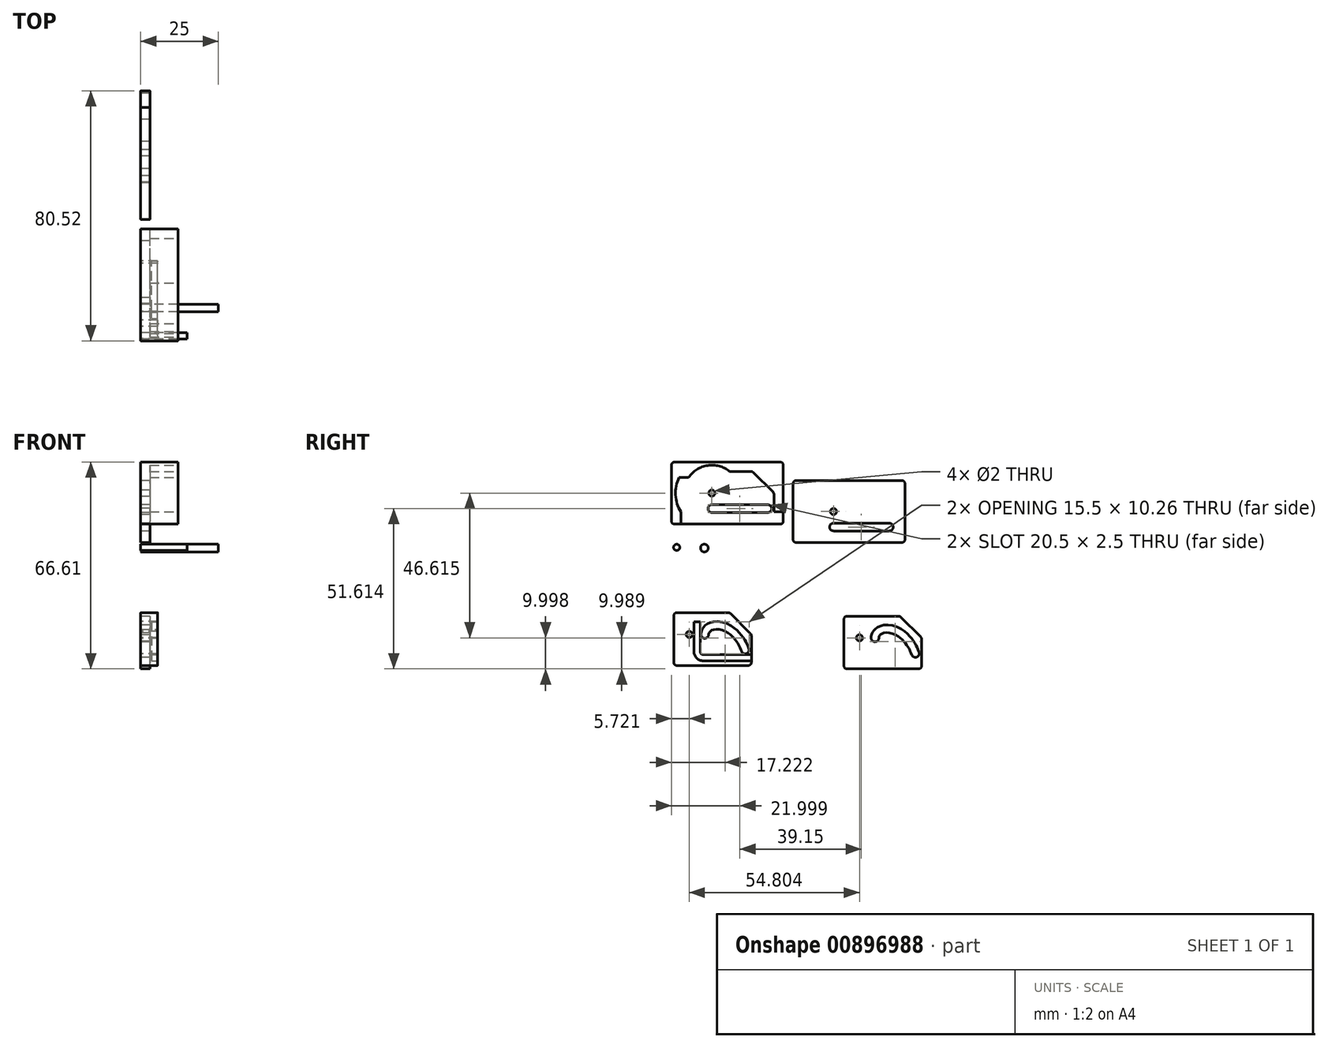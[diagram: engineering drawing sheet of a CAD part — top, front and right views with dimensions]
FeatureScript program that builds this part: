
annotation { "Feature Type Name" : "Feature", "Feature Type Description" : "" }
export const myFeature = defineFeature(function(context is Context, id is Id, definition is map)
    precondition{}
    {
        {
            var Q0;
            Q0=qCreatedBy(makeId("Right.planeOp"),FACE);
            var sketch = newSketch(context, id + "F0", { "sketchPlane" : qUnion([Q0])});
            skLineSegment(sketch, "E0.bottom", {"start": v(-142.35, 68.58) * mm, "end": v(-108.35, 68.58) * mm});
            skLineSegment(sketch, "E0.top", {"start": v(-142.35, 48.58) * mm, "end": v(-108.35, 48.58) * mm});
            skLineSegment(sketch, "E0.left", {"start": v(-143.35, 67.58) * mm, "end": v(-143.35, 49.58) * mm});
            skLineSegment(sketch, "E0.right", {"start": v(-107.35, 67.58) * mm, "end": v(-107.35, 49.58) * mm});
            skLineSegment(sketch, "E1", {"start": v(-130.35, 53.58) * mm, "end": v(-112.35, 53.58) * mm, "construction": true});
            skCircle(sketch, "E2", {"center": v(-130.35, 58.58) * mm, "radius": 1 * mm});
            skArc(sketch, "E3.0.startCap", {"start": v(-130.35, 52.33) * mm, "mid": v(-131.6, 53.58) * mm, "end": v(-130.35, 54.83) * mm});
            skArc(sketch, "E3.0.endCap", {"start": v(-112.35, 54.83) * mm, "mid": v(-111.1, 53.58) * mm, "end": v(-112.35, 52.33) * mm});
            skLineSegment(sketch, "E3.0.left", {"start": v(-130.35, 54.83) * mm, "end": v(-112.35, 54.83) * mm});
            skLineSegment(sketch, "E3.0.right", {"start": v(-130.35, 52.33) * mm, "end": v(-112.35, 52.33) * mm});
            skCircle(sketch, "E4", {"center": v(-176.78, 19) * mm, "radius": 1 * mm});
            skLineSegment(sketch, "E5", {"start": v(-180.78, 9) * mm, "end": v(-157.78, 9) * mm});
            skLineSegment(sketch, "E6", {"start": v(-181.78, 10) * mm, "end": v(-181.78, 25) * mm});
            skLineSegment(sketch, "E7", {"start": v(-180.78, 26) * mm, "end": v(-164.2, 26) * mm});
            skLineSegment(sketch, "E8", {"start": v(-156.78, 18.59) * mm, "end": v(-156.78, 10) * mm});
            skPoint(sketch, "E9", {"position": v(-171.78, 19) * mm});
            skPoint(sketch, "E10", {"position": v(-171.71, 19.56) * mm});
            skPoint(sketch, "E11", {"position": v(-171.5, 20.1) * mm});
            skPoint(sketch, "E12", {"position": v(-171.17, 20.6) * mm});
            skPoint(sketch, "E13", {"position": v(-170.71, 21.05) * mm});
            skPoint(sketch, "E14", {"position": v(-170.13, 21.42) * mm});
            skPoint(sketch, "E15", {"position": v(-169.45, 21.7) * mm});
            skPoint(sketch, "E16", {"position": v(-168.67, 21.87) * mm});
            skPoint(sketch, "E17", {"position": v(-167.8, 21.91) * mm});
            skPoint(sketch, "E18", {"position": v(-166.88, 21.83) * mm});
            skPoint(sketch, "E19", {"position": v(-165.9, 21.6) * mm});
            skPoint(sketch, "E20", {"position": v(-164.9, 21.21) * mm});
            skPoint(sketch, "E21", {"position": v(-163.89, 20.67) * mm});
            skPoint(sketch, "E22", {"position": v(-162.88, 19.96) * mm});
            skPoint(sketch, "E23", {"position": v(-161.91, 19.09) * mm});
            skPoint(sketch, "E24", {"position": v(-161, 18.05) * mm});
            skPoint(sketch, "E25", {"position": v(-160.15, 16.85) * mm});
            skPoint(sketch, "E26", {"position": v(-159.4, 15.5) * mm});
            skPoint(sketch, "E27", {"position": v(-158.78, 14) * mm});
            skFitSpline(sketch, "E28", {"points": [v(-171.78, 19) * mm, v(-171.71, 19.56) * mm, v(-171.5, 20.1) * mm, v(-171.17, 20.6) * mm, v(-170.71, 21.05) * mm, v(-170.13, 21.42) * mm, v(-169.45, 21.7) * mm, v(-168.67, 21.87) * mm, v(-167.8, 21.91) * mm, v(-166.88, 21.83) * mm, v(-165.9, 21.6) * mm, v(-164.9, 21.21) * mm, v(-163.89, 20.67) * mm, v(-162.88, 19.96) * mm, v(-161.91, 19.09) * mm, v(-161, 18.05) * mm, v(-160.15, 16.85) * mm, v(-159.4, 15.5) * mm, v(-158.78, 14) * mm], "startDerivative": vector(0.94, 13.4) * mm, "endDerivative": vector(8.38, -21.3) * mm});
            skArc(sketch, "E29.0.startCap", {"start": v(-170.53, 18.91) * mm, "mid": v(-171.87, 17.75) * mm, "end": v(-173.03, 19.09) * mm});
            skArc(sketch, "E29.0.endCap", {"start": v(-157.62, 14.46) * mm, "mid": v(-158.32, 12.84) * mm, "end": v(-159.94, 13.54) * mm});
            skFitSpline(sketch, "E29.0.left", {"points": [v(-173.03, 19.09) * mm, v(-173.02, 19.12) * mm, v(-173.02, 19.2) * mm, v(-173, 19.32) * mm, v(-173, 19.46) * mm, v(-172.97, 19.6) * mm, v(-172.95, 19.73) * mm, v(-172.94, 19.81) * mm, v(-172.92, 19.87) * mm, v(-172.9, 19.94) * mm, v(-172.88, 20.02) * mm, v(-172.85, 20.13) * mm, v(-172.79, 20.31) * mm, v(-172.71, 20.49) * mm, v(-172.64, 20.63) * mm, v(-172.6, 20.72) * mm, v(-172.5, 20.88) * mm, v(-172.37, 21.1) * mm, v(-172.21, 21.31) * mm, v(-172.07, 21.47) * mm, v(-171.93, 21.63) * mm, v(-171.75, 21.81) * mm, v(-171.5, 22.02) * mm, v(-171.18, 22.26) * mm, v(-170.73, 22.53) * mm, v(-170.16, 22.79) * mm, v(-169.56, 22.97) * mm, v(-168.74, 23.14) * mm, v(-167.69, 23.2) * mm, v(-166.4, 23.05) * mm, v(-165.14, 22.7) * mm, v(-163.9, 22.15) * mm, v(-162.93, 21.56) * mm, v(-162.18, 21) * mm, v(-161.64, 20.56) * mm, v(-161.12, 20.07) * mm, v(-160.62, 19.56) * mm, v(-160.23, 19.1) * mm, v(-159.93, 18.72) * mm, v(-159.63, 18.33) * mm, v(-159.35, 17.92) * mm, v(-159.09, 17.5) * mm, v(-158.9, 17.19) * mm, v(-158.7, 16.86) * mm, v(-158.52, 16.53) * mm, v(-158.38, 16.24) * mm, v(-158.26, 16) * mm, v(-158.16, 15.77) * mm, v(-158.03, 15.48) * mm, v(-157.84, 15.02) * mm, v(-157.7, 14.68) * mm, v(-157.62, 14.46) * mm]});
            skFitSpline(sketch, "E29.0.right", {"points": [v(-170.53, 18.91) * mm, v(-170.53, 18.95) * mm, v(-170.53, 19.01) * mm, v(-170.52, 19.1) * mm, v(-170.51, 19.17) * mm, v(-170.5, 19.23) * mm, v(-170.5, 19.26) * mm, v(-170.5, 19.28) * mm, v(-170.5, 19.3) * mm, v(-170.49, 19.3) * mm, v(-170.48, 19.32) * mm, v(-170.47, 19.35) * mm, v(-170.46, 19.4) * mm, v(-170.43, 19.46) * mm, v(-170.4, 19.5) * mm, v(-170.4, 19.54) * mm, v(-170.37, 19.58) * mm, v(-170.34, 19.64) * mm, v(-170.3, 19.7) * mm, v(-170.24, 19.77) * mm, v(-170.2, 19.83) * mm, v(-170.13, 19.9) * mm, v(-170.06, 19.97) * mm, v(-169.95, 20.06) * mm, v(-169.8, 20.17) * mm, v(-169.58, 20.3) * mm, v(-169.28, 20.44) * mm, v(-168.94, 20.55) * mm, v(-168.45, 20.65) * mm, v(-167.78, 20.69) * mm, v(-166.9, 20.59) * mm, v(-165.99, 20.33) * mm, v(-165.07, 19.93) * mm, v(-164.31, 19.47) * mm, v(-163.73, 19.04) * mm, v(-163.3, 18.68) * mm, v(-162.88, 18.3) * mm, v(-162.48, 17.87) * mm, v(-162.15, 17.5) * mm, v(-161.9, 17.19) * mm, v(-161.66, 16.87) * mm, v(-161.43, 16.53) * mm, v(-161.2, 16.18) * mm, v(-161.04, 15.91) * mm, v(-160.89, 15.64) * mm, v(-160.74, 15.37) * mm, v(-160.62, 15.13) * mm, v(-160.53, 14.94) * mm, v(-160.44, 14.75) * mm, v(-160.33, 14.5) * mm, v(-160.16, 14.1) * mm, v(-160.03, 13.76) * mm, v(-159.94, 13.54) * mm]});
            skCircle(sketch, "E30", {"center": v(-171.91, 46.81) * mm, "radius": 1.25 * mm});
            skCircle(sketch, "E31", {"center": v(-180.83, 47.04) * mm, "radius": 1 * mm});
            skLineSegment(sketch, "E32", {"start": v(-163.49, 25.7) * mm, "end": v(-157.07, 19.3) * mm});
            skCircle(sketch, "E33", {"center": v(-121.98, 17.89) * mm, "radius": 1 * mm});
            skLineSegment(sketch, "E34", {"start": v(-125.98, 7.89) * mm, "end": v(-102.98, 7.89) * mm});
            skLineSegment(sketch, "E35", {"start": v(-126.98, 8.89) * mm, "end": v(-126.98, 23.89) * mm});
            skLineSegment(sketch, "E36", {"start": v(-125.98, 24.89) * mm, "end": v(-109.39, 24.89) * mm});
            skPoint(sketch, "E37", {"position": v(-116.98, 17.89) * mm});
            skPoint(sketch, "E38", {"position": v(-116.9, 18.45) * mm});
            skPoint(sketch, "E39", {"position": v(-116.7, 18.99) * mm});
            skPoint(sketch, "E40", {"position": v(-116.37, 19.5) * mm});
            skPoint(sketch, "E41", {"position": v(-115.9, 19.94) * mm});
            skPoint(sketch, "E42", {"position": v(-115.33, 20.3) * mm});
            skPoint(sketch, "E43", {"position": v(-114.65, 20.58) * mm});
            skPoint(sketch, "E44", {"position": v(-113.86, 20.75) * mm});
            skPoint(sketch, "E45", {"position": v(-113, 20.8) * mm});
            skPoint(sketch, "E46", {"position": v(-112.08, 20.72) * mm});
            skPoint(sketch, "E47", {"position": v(-111.1, 20.49) * mm});
            skPoint(sketch, "E48", {"position": v(-110.1, 20.1) * mm});
            skPoint(sketch, "E49", {"position": v(-109.08, 19.56) * mm});
            skPoint(sketch, "E50", {"position": v(-108.08, 18.85) * mm});
            skPoint(sketch, "E51", {"position": v(-107.1, 17.98) * mm});
            skPoint(sketch, "E52", {"position": v(-106.2, 16.94) * mm});
            skPoint(sketch, "E53", {"position": v(-105.35, 15.74) * mm});
            skPoint(sketch, "E54", {"position": v(-104.6, 14.39) * mm});
            skPoint(sketch, "E55", {"position": v(-103.98, 12.89) * mm});
            skFitSpline(sketch, "E56", {"points": [v(-116.98, 17.89) * mm, v(-116.9, 18.45) * mm, v(-116.7, 18.99) * mm, v(-116.37, 19.5) * mm, v(-115.9, 19.94) * mm, v(-115.33, 20.3) * mm, v(-114.65, 20.58) * mm, v(-113.86, 20.75) * mm, v(-113, 20.8) * mm, v(-112.08, 20.72) * mm, v(-111.1, 20.49) * mm, v(-110.1, 20.1) * mm, v(-109.08, 19.56) * mm, v(-108.08, 18.85) * mm, v(-107.1, 17.98) * mm, v(-106.2, 16.94) * mm, v(-105.35, 15.74) * mm, v(-104.6, 14.39) * mm, v(-103.98, 12.89) * mm], "startDerivative": vector(0.94, 13.4) * mm, "endDerivative": vector(8.38, -21.3) * mm});
            skArc(sketch, "E57.0.startCap", {"start": v(-115.73, 17.8) * mm, "mid": v(-117.06, 16.64) * mm, "end": v(-118.22, 17.98) * mm});
            skArc(sketch, "E57.0.endCap", {"start": v(-102.81, 13.35) * mm, "mid": v(-103.52, 11.73) * mm, "end": v(-105.14, 12.43) * mm});
            skFitSpline(sketch, "E57.0.left", {"points": [v(-118.22, 17.98) * mm, v(-118.22, 18.01) * mm, v(-118.21, 18.09) * mm, v(-118.2, 18.2) * mm, v(-118.2, 18.35) * mm, v(-118.17, 18.5) * mm, v(-118.15, 18.62) * mm, v(-118.13, 18.7) * mm, v(-118.12, 18.76) * mm, v(-118.1, 18.83) * mm, v(-118.08, 18.91) * mm, v(-118.05, 19.02) * mm, v(-117.98, 19.2) * mm, v(-117.9, 19.38) * mm, v(-117.84, 19.52) * mm, v(-117.8, 19.61) * mm, v(-117.7, 19.77) * mm, v(-117.56, 20) * mm, v(-117.4, 20.2) * mm, v(-117.27, 20.36) * mm, v(-117.13, 20.52) * mm, v(-116.94, 20.7) * mm, v(-116.7, 20.9) * mm, v(-116.37, 21.15) * mm, v(-115.93, 21.42) * mm, v(-115.36, 21.67) * mm, v(-114.76, 21.86) * mm, v(-113.94, 22.03) * mm, v(-112.88, 22.09) * mm, v(-111.6, 21.93) * mm, v(-110.33, 21.58) * mm, v(-109.1, 21.04) * mm, v(-108.12, 20.45) * mm, v(-107.38, 19.9) * mm, v(-106.84, 19.45) * mm, v(-106.32, 18.96) * mm, v(-105.82, 18.45) * mm, v(-105.43, 17.99) * mm, v(-105.12, 17.6) * mm, v(-104.83, 17.21) * mm, v(-104.55, 16.81) * mm, v(-104.28, 16.4) * mm, v(-104.09, 16.08) * mm, v(-103.9, 15.75) * mm, v(-103.72, 15.42) * mm, v(-103.57, 15.13) * mm, v(-103.46, 14.9) * mm, v(-103.35, 14.66) * mm, v(-103.23, 14.37) * mm, v(-103.03, 13.9) * mm, v(-102.9, 13.57) * mm, v(-102.81, 13.35) * mm]});
            skFitSpline(sketch, "E57.0.right", {"points": [v(-115.73, 17.8) * mm, v(-115.73, 17.84) * mm, v(-115.72, 17.9) * mm, v(-115.71, 17.99) * mm, v(-115.7, 18.06) * mm, v(-115.7, 18.12) * mm, v(-115.7, 18.15) * mm, v(-115.69, 18.17) * mm, v(-115.69, 18.18) * mm, v(-115.68, 18.2) * mm, v(-115.68, 18.21) * mm, v(-115.67, 18.24) * mm, v(-115.65, 18.29) * mm, v(-115.63, 18.34) * mm, v(-115.6, 18.4) * mm, v(-115.59, 18.43) * mm, v(-115.56, 18.47) * mm, v(-115.53, 18.52) * mm, v(-115.49, 18.6) * mm, v(-115.44, 18.66) * mm, v(-115.39, 18.72) * mm, v(-115.33, 18.78) * mm, v(-115.25, 18.86) * mm, v(-115.15, 18.95) * mm, v(-115, 19.06) * mm, v(-114.77, 19.2) * mm, v(-114.47, 19.33) * mm, v(-114.14, 19.44) * mm, v(-113.65, 19.54) * mm, v(-112.97, 19.58) * mm, v(-112.1, 19.47) * mm, v(-111.18, 19.22) * mm, v(-110.26, 18.82) * mm, v(-109.5, 18.36) * mm, v(-108.92, 17.93) * mm, v(-108.5, 17.57) * mm, v(-108.07, 17.18) * mm, v(-107.67, 16.76) * mm, v(-107.35, 16.39) * mm, v(-107.1, 16.08) * mm, v(-106.86, 15.76) * mm, v(-106.63, 15.42) * mm, v(-106.4, 15.07) * mm, v(-106.24, 14.8) * mm, v(-106.08, 14.53) * mm, v(-105.93, 14.25) * mm, v(-105.81, 14.02) * mm, v(-105.72, 13.83) * mm, v(-105.63, 13.64) * mm, v(-105.53, 13.4) * mm, v(-105.35, 12.98) * mm, v(-105.23, 12.65) * mm, v(-105.14, 12.43) * mm]});
            skLineSegment(sketch, "E58", {"start": v(-108.68, 24.6) * mm, "end": v(-102.27, 18.18) * mm});
            skPoint(sketch, "E59.visualSharp", {"position": v(-143.35, 68.58) * mm});
            skArc(sketch, "E59.filletArc", {"start": v(-142.35, 68.58) * mm, "mid": v(-143.06, 68.28) * mm, "end": v(-143.35, 67.58) * mm});
            skPoint(sketch, "E60.visualSharp", {"position": v(-143.35, 48.58) * mm});
            skArc(sketch, "E60.filletArc", {"start": v(-143.35, 49.58) * mm, "mid": v(-143.06, 48.87) * mm, "end": v(-142.35, 48.58) * mm});
            skPoint(sketch, "E61.visualSharp", {"position": v(-107.35, 48.58) * mm});
            skArc(sketch, "E61.filletArc", {"start": v(-108.35, 48.58) * mm, "mid": v(-107.64, 48.87) * mm, "end": v(-107.35, 49.58) * mm});
            skPoint(sketch, "E62.visualSharp", {"position": v(-107.35, 68.58) * mm});
            skArc(sketch, "E62.filletArc", {"start": v(-107.35, 67.58) * mm, "mid": v(-107.64, 68.28) * mm, "end": v(-108.35, 68.58) * mm});
            skPoint(sketch, "E63.visualSharp", {"position": v(-181.78, 26) * mm});
            skArc(sketch, "E63.filletArc", {"start": v(-180.78, 26) * mm, "mid": v(-181.49, 25.7) * mm, "end": v(-181.78, 25) * mm});
            skPoint(sketch, "E64.visualSharp", {"position": v(-181.78, 9) * mm});
            skArc(sketch, "E64.filletArc", {"start": v(-181.78, 10) * mm, "mid": v(-181.49, 9.3) * mm, "end": v(-180.78, 9) * mm});
            skPoint(sketch, "E65.visualSharp", {"position": v(-156.78, 9) * mm});
            skArc(sketch, "E65.filletArc", {"start": v(-157.78, 9) * mm, "mid": v(-157.07, 9.3) * mm, "end": v(-156.78, 10) * mm});
            skPoint(sketch, "E66.visualSharp", {"position": v(-156.78, 19) * mm});
            skArc(sketch, "E66.filletArc", {"start": v(-156.78, 18.59) * mm, "mid": v(-156.86, 18.97) * mm, "end": v(-157.07, 19.3) * mm});
            skPoint(sketch, "E67.visualSharp", {"position": v(-163.78, 26) * mm});
            skArc(sketch, "E67.filletArc", {"start": v(-163.49, 25.7) * mm, "mid": v(-163.81, 25.92) * mm, "end": v(-164.2, 26) * mm});
            skPoint(sketch, "E68.visualSharp", {"position": v(-126.98, 24.89) * mm});
            skArc(sketch, "E68.filletArc", {"start": v(-125.98, 24.89) * mm, "mid": v(-126.68, 24.6) * mm, "end": v(-126.98, 23.89) * mm});
            skPoint(sketch, "E69.visualSharp", {"position": v(-126.98, 7.89) * mm});
            skArc(sketch, "E69.filletArc", {"start": v(-126.98, 8.89) * mm, "mid": v(-126.68, 8.18) * mm, "end": v(-125.98, 7.89) * mm});
            skPoint(sketch, "E70.visualSharp", {"position": v(-101.98, 7.89) * mm});
            skArc(sketch, "E70.filletArc", {"start": v(-102.98, 7.89) * mm, "mid": v(-102.27, 8.18) * mm, "end": v(-101.98, 8.89) * mm});
            skPoint(sketch, "E71.visualSharp", {"position": v(-101.98, 17.89) * mm});
            skArc(sketch, "E71.filletArc", {"start": v(-101.98, 17.47) * mm, "mid": v(-102.05, 17.86) * mm, "end": v(-102.27, 18.18) * mm});
            skPoint(sketch, "E72.visualSharp", {"position": v(-108.98, 24.89) * mm});
            skArc(sketch, "E72.filletArc", {"start": v(-108.68, 24.6) * mm, "mid": v(-109, 24.81) * mm, "end": v(-109.39, 24.89) * mm});
            skLineSegment(sketch, "E73", {"start": v(-293, 71.05) * mm, "end": v(-291, 71.05) * mm});
            skLineSegment(sketch, "E74", {"start": v(-291, 71.05) * mm, "end": v(-291, 61.55) * mm});
            skLineSegment(sketch, "E75", {"start": v(-290, 60.55) * mm, "end": v(-206, 60.55) * mm});
            skLineSegment(sketch, "E76", {"start": v(-205, 61.55) * mm, "end": v(-205, 83.55) * mm});
            skLineSegment(sketch, "E77", {"start": v(-205, 83.55) * mm, "end": v(-203, 83.55) * mm});
            skLineSegment(sketch, "E78", {"start": v(-203, 83.55) * mm, "end": v(-203, 61.55) * mm});
            skLineSegment(sketch, "E79", {"start": v(-206, 58.55) * mm, "end": v(-290, 58.55) * mm});
            skLineSegment(sketch, "E80", {"start": v(-293, 61.55) * mm, "end": v(-293, 71.05) * mm});
            skPoint(sketch, "E81.visualSharp", {"position": v(-291, 60.55) * mm});
            skArc(sketch, "E81.filletArc", {"start": v(-291, 61.55) * mm, "mid": v(-290.7, 60.84) * mm, "end": v(-290, 60.55) * mm});
            skPoint(sketch, "E82.visualSharp", {"position": v(-205, 60.55) * mm});
            skArc(sketch, "E82.filletArc", {"start": v(-206, 60.55) * mm, "mid": v(-205.3, 60.84) * mm, "end": v(-205, 61.55) * mm});
            skPoint(sketch, "E83.visualSharp", {"position": v(-203, 58.55) * mm});
            skArc(sketch, "E83.filletArc", {"start": v(-206, 58.55) * mm, "mid": v(-203.88, 59.43) * mm, "end": v(-203, 61.55) * mm});
            skPoint(sketch, "E84.visualSharp", {"position": v(-293, 58.55) * mm});
            skArc(sketch, "E84.filletArc", {"start": v(-293, 61.55) * mm, "mid": v(-292.12, 59.43) * mm, "end": v(-290, 58.55) * mm});
            skLineSegment(sketch, "E85", {"start": v(-292, 71.05) * mm, "end": v(-292, 61.55) * mm});
            skLineSegment(sketch, "E86", {"start": v(-290, 59.55) * mm, "end": v(-206, 59.55) * mm});
            skLineSegment(sketch, "E87", {"start": v(-204, 61.55) * mm, "end": v(-204, 83.55) * mm});
            skPoint(sketch, "E88.visualSharp", {"position": v(-204, 59.55) * mm});
            skArc(sketch, "E88.filletArc", {"start": v(-206, 59.55) * mm, "mid": v(-204.59, 60.14) * mm, "end": v(-204, 61.55) * mm});
            skPoint(sketch, "E89.visualSharp", {"position": v(-292, 59.55) * mm});
            skArc(sketch, "E89.filletArc", {"start": v(-292, 61.55) * mm, "mid": v(-291.42, 60.14) * mm, "end": v(-290, 59.55) * mm});
            skLineSegment(sketch, "E90", {"start": v(-101.98, 17.47) * mm, "end": v(-101.98, 8.89) * mm});
            skLineSegment(sketch, "E91.bottom", {"start": v(-181.5, 74.5) * mm, "end": v(-147.5, 74.5) * mm});
            skLineSegment(sketch, "E91.top", {"start": v(-181.5, 54.5) * mm, "end": v(-147.5, 54.5) * mm});
            skLineSegment(sketch, "E91.left", {"start": v(-182.5, 73.5) * mm, "end": v(-182.5, 55.5) * mm});
            skLineSegment(sketch, "E91.right", {"start": v(-146.5, 73.5) * mm, "end": v(-146.5, 55.5) * mm});
            skLineSegment(sketch, "E92", {"start": v(-169.5, 59.5) * mm, "end": v(-151.5, 59.5) * mm, "construction": true});
            skCircle(sketch, "E93", {"center": v(-169.5, 64.5) * mm, "radius": 1 * mm});
            skArc(sketch, "E94.0.startCap", {"start": v(-169.5, 58.25) * mm, "mid": v(-170.75, 59.5) * mm, "end": v(-169.5, 60.75) * mm});
            skArc(sketch, "E94.0.endCap", {"start": v(-151.5, 60.75) * mm, "mid": v(-150.25, 59.5) * mm, "end": v(-151.5, 58.25) * mm});
            skLineSegment(sketch, "E94.0.left", {"start": v(-169.5, 60.75) * mm, "end": v(-151.5, 60.75) * mm});
            skLineSegment(sketch, "E94.0.right", {"start": v(-169.5, 58.25) * mm, "end": v(-151.5, 58.25) * mm});
            skPoint(sketch, "E95.visualSharp", {"position": v(-182.5, 74.5) * mm});
            skArc(sketch, "E95.filletArc", {"start": v(-181.5, 74.5) * mm, "mid": v(-182.2, 74.21) * mm, "end": v(-182.5, 73.5) * mm});
            skPoint(sketch, "E96.visualSharp", {"position": v(-182.5, 54.5) * mm});
            skArc(sketch, "E96.filletArc", {"start": v(-182.5, 55.5) * mm, "mid": v(-182.2, 54.8) * mm, "end": v(-181.5, 54.5) * mm});
            skPoint(sketch, "E97.visualSharp", {"position": v(-146.5, 54.5) * mm});
            skArc(sketch, "E97.filletArc", {"start": v(-147.5, 54.5) * mm, "mid": v(-146.8, 54.8) * mm, "end": v(-146.5, 55.5) * mm});
            skPoint(sketch, "E98.visualSharp", {"position": v(-146.5, 74.5) * mm});
            skArc(sketch, "E98.filletArc", {"start": v(-146.5, 73.5) * mm, "mid": v(-146.8, 74.21) * mm, "end": v(-147.5, 74.5) * mm});
            skSolve(sketch);
        }
        {
            var Q0;
            Q0=makeQuery(id+"F0.imprint","IMPRINT",FACE,{"disambiguationData":[TD([[makeQuery(id+"F0.imprint","IMPRINT",EDGE,{"derivedFrom":sQuery(id+"F0.wireOp",EDGE,"E0.bottom")}),-1.0]])]});
            extrude(context, id + "F1", {"entities" : qUnion([Q0]), "depth" : 3 * mm, "offsetDistance" : 25 * mm});
        }
        {
            var Q0;
            Q0=makeQuery(id+"F0.imprint","IMPRINT",FACE,{"disambiguationData":[TD([[makeQuery(id+"F0.imprint","IMPRINT",EDGE,{"derivedFrom":sQuery(id+"F0.wireOp",EDGE,"E4")}),-1.0]])]});
            extrude(context, id + "F2", {"entities" : qUnion([Q0]), "operationType" : NewBodyOperationType.ADD, "depth" : 5.5 * mm, "offsetDistance" : 25 * mm});
        }
        {
            var Q0;
            Q0=makeQuery(id+"F0.imprint","IMPRINT",FACE,{"disambiguationData":[TD([[makeQuery(id+"F0.imprint","IMPRINT",EDGE,{"derivedFrom":sQuery(id+"F0.wireOp",EDGE,"E31")}),1.0]])]});
            extrude(context, id + "F3", {"entities" : qUnion([Q0]), "depth" : 15 * mm, "offsetDistance" : 25 * mm});
        }
        {
            var Q0;
            Q0=makeQuery(id+"F0.imprint","IMPRINT",FACE,{"disambiguationData":[TD([[makeQuery(id+"F0.imprint","IMPRINT",EDGE,{"derivedFrom":sQuery(id+"F0.wireOp",EDGE,"E30")}),1.0]])]});
            extrude(context, id + "F4", {"entities" : qUnion([Q0]), "depth" : 25 * mm, "offsetDistance" : 25 * mm});
        }
        {
            var Q0;
            Q0=makeQuery(id+"F0.imprint","IMPRINT",FACE,{"disambiguationData":[TD([[makeQuery(id+"F0.imprint","IMPRINT",EDGE,{"derivedFrom":sQuery(id+"F0.wireOp",EDGE,"E33")}),-1.0]])]});
            extrude(context, id + "F5", {"entities" : qUnion([Q0]), "depth" : 3 * mm, "offsetDistance" : 25 * mm});
        }
        {
            var Q0;
            Q0=makeQuery(id+"F2.opExtrude","CAP_FACE",FACE,{"disambiguationData":[OSD([sQuery(id+"F0.wireOp",EDGE,"E4"),sQuery(id+"F0.wireOp",EDGE,"E5"),sQuery(id+"F0.wireOp",EDGE,"E6"),sQuery(id+"F0.wireOp",EDGE,"E7"),sQuery(id+"F0.wireOp",EDGE,"E8"),sQuery(id+"F0.wireOp",EDGE,"E29.0.startCap"),sQuery(id+"F0.wireOp",EDGE,"E29.0.endCap"),sQuery(id+"F0.wireOp",EDGE,"E29.0.left"),sQuery(id+"F0.wireOp",EDGE,"E29.0.right"),sQuery(id+"F0.wireOp",EDGE,"E32"),sQuery(id+"F0.wireOp",EDGE,"E63.filletArc"),sQuery(id+"F0.wireOp",EDGE,"E64.filletArc"),sQuery(id+"F0.wireOp",EDGE,"E65.filletArc"),sQuery(id+"F0.wireOp",EDGE,"E66.filletArc"),sQuery(id+"F0.wireOp",EDGE,"E67.filletArc")])],"isStart":false});
            var sketch = newSketch(context, id + "F6", { "sketchPlane" : qUnion([Q0])});
            skCircle(sketch, "E99", {"center": v(-176.78, 19) * mm, "radius": 1 * mm});
            skLineSegment(sketch, "E100", {"start": v(-180.78, 9) * mm, "end": v(-157.78, 9) * mm});
            skLineSegment(sketch, "E101", {"start": v(-181.78, 10) * mm, "end": v(-181.78, 25) * mm});
            skLineSegment(sketch, "E102", {"start": v(-180.78, 26) * mm, "end": v(-164.2, 26) * mm});
            skLineSegment(sketch, "E103", {"start": v(-156.78, 18.59) * mm, "end": v(-156.78, 12.5) * mm});
            skPoint(sketch, "E104", {"position": v(-171.78, 19) * mm});
            skPoint(sketch, "E105", {"position": v(-171.71, 19.56) * mm});
            skPoint(sketch, "E106", {"position": v(-171.5, 20.1) * mm});
            skPoint(sketch, "E107", {"position": v(-171.17, 20.6) * mm});
            skPoint(sketch, "E108", {"position": v(-170.71, 21.05) * mm});
            skPoint(sketch, "E109", {"position": v(-170.13, 21.42) * mm});
            skPoint(sketch, "E110", {"position": v(-169.45, 21.7) * mm});
            skPoint(sketch, "E111", {"position": v(-168.67, 21.87) * mm});
            skPoint(sketch, "E112", {"position": v(-167.8, 21.91) * mm});
            skPoint(sketch, "E113", {"position": v(-166.88, 21.83) * mm});
            skPoint(sketch, "E114", {"position": v(-165.9, 21.6) * mm});
            skPoint(sketch, "E115", {"position": v(-164.9, 21.21) * mm});
            skPoint(sketch, "E116", {"position": v(-163.89, 20.67) * mm});
            skPoint(sketch, "E117", {"position": v(-162.88, 19.96) * mm});
            skPoint(sketch, "E118", {"position": v(-161.91, 19.09) * mm});
            skPoint(sketch, "E119", {"position": v(-161, 18.05) * mm});
            skPoint(sketch, "E120", {"position": v(-160.15, 16.85) * mm});
            skPoint(sketch, "E121", {"position": v(-159.4, 15.5) * mm});
            skPoint(sketch, "E122", {"position": v(-158.78, 14) * mm});
            skFitSpline(sketch, "E123", {"points": [v(-171.78, 19) * mm, v(-171.71, 19.56) * mm, v(-171.5, 20.1) * mm, v(-171.17, 20.6) * mm, v(-170.71, 21.05) * mm, v(-170.13, 21.42) * mm, v(-169.45, 21.7) * mm, v(-168.67, 21.87) * mm, v(-167.8, 21.91) * mm, v(-166.88, 21.83) * mm, v(-165.9, 21.6) * mm, v(-164.9, 21.21) * mm, v(-163.89, 20.67) * mm, v(-162.88, 19.96) * mm, v(-161.91, 19.09) * mm, v(-161, 18.05) * mm, v(-160.15, 16.85) * mm, v(-159.4, 15.5) * mm, v(-158.78, 14) * mm], "startDerivative": vector(0.94, 13.4) * mm, "endDerivative": vector(8.38, -21.3) * mm});
            skArc(sketch, "E124.0.startCap", {"start": v(-170.78, 18.93) * mm, "mid": v(-171.85, 18) * mm, "end": v(-172.78, 19.07) * mm});
            skArc(sketch, "E124.0.endCap", {"start": v(-157.85, 14.37) * mm, "mid": v(-158.41, 13.07) * mm, "end": v(-159.7, 13.63) * mm});
            skFitSpline(sketch, "E124.0.left", {"points": [v(-172.78, 19.07) * mm, v(-172.77, 19.14) * mm, v(-172.76, 19.26) * mm, v(-172.75, 19.43) * mm, v(-172.73, 19.57) * mm, v(-172.7, 19.68) * mm, v(-172.7, 19.76) * mm, v(-172.68, 19.81) * mm, v(-172.66, 19.88) * mm, v(-172.64, 19.95) * mm, v(-172.61, 20.05) * mm, v(-172.55, 20.22) * mm, v(-172.47, 20.4) * mm, v(-172.39, 20.58) * mm, v(-172.3, 20.75) * mm, v(-172.16, 20.96) * mm, v(-172.01, 21.16) * mm, v(-171.89, 21.3) * mm, v(-171.75, 21.46) * mm, v(-171.58, 21.63) * mm, v(-171.35, 21.82) * mm, v(-171.04, 22.06) * mm, v(-170.61, 22.3) * mm, v(-170.07, 22.55) * mm, v(-169.5, 22.73) * mm, v(-168.71, 22.9) * mm, v(-167.7, 22.95) * mm, v(-166.45, 22.8) * mm, v(-165.22, 22.46) * mm, v(-164.02, 21.93) * mm, v(-163.07, 21.35) * mm, v(-162.34, 20.81) * mm, v(-161.8, 20.37) * mm, v(-161.3, 19.9) * mm, v(-160.8, 19.39) * mm, v(-160.35, 18.85) * mm, v(-159.9, 18.28) * mm, v(-159.56, 17.78) * mm, v(-159.3, 17.37) * mm, v(-159.1, 17.06) * mm, v(-158.92, 16.74) * mm, v(-158.74, 16.41) * mm, v(-158.6, 16.13) * mm, v(-158.5, 15.9) * mm, v(-158.38, 15.67) * mm, v(-158.26, 15.38) * mm, v(-158.07, 14.93) * mm, v(-157.94, 14.59) * mm, v(-157.85, 14.37) * mm]});
            skFitSpline(sketch, "E124.0.right", {"points": [v(-170.78, 18.93) * mm, v(-170.78, 19) * mm, v(-170.77, 19.1) * mm, v(-170.76, 19.2) * mm, v(-170.75, 19.27) * mm, v(-170.74, 19.3) * mm, v(-170.74, 19.33) * mm, v(-170.73, 19.35) * mm, v(-170.73, 19.37) * mm, v(-170.72, 19.4) * mm, v(-170.71, 19.43) * mm, v(-170.69, 19.5) * mm, v(-170.66, 19.57) * mm, v(-170.62, 19.65) * mm, v(-170.57, 19.73) * mm, v(-170.51, 19.83) * mm, v(-170.44, 19.92) * mm, v(-170.38, 20) * mm, v(-170.31, 20.07) * mm, v(-170.23, 20.15) * mm, v(-170.1, 20.26) * mm, v(-169.93, 20.38) * mm, v(-169.7, 20.53) * mm, v(-169.36, 20.68) * mm, v(-169, 20.8) * mm, v(-168.48, 20.9) * mm, v(-167.77, 20.94) * mm, v(-166.85, 20.83) * mm, v(-165.9, 20.57) * mm, v(-164.95, 20.15) * mm, v(-164.17, 19.68) * mm, v(-163.57, 19.24) * mm, v(-163.13, 18.87) * mm, v(-162.7, 18.47) * mm, v(-162.3, 18.04) * mm, v(-161.9, 17.58) * mm, v(-161.52, 17.1) * mm, v(-161.22, 16.67) * mm, v(-161, 16.31) * mm, v(-160.83, 16.04) * mm, v(-160.67, 15.76) * mm, v(-160.51, 15.48) * mm, v(-160.4, 15.24) * mm, v(-160.3, 15.05) * mm, v(-160.21, 14.85) * mm, v(-160.1, 14.6) * mm, v(-159.93, 14.18) * mm, v(-159.8, 13.86) * mm, v(-159.7, 13.63) * mm]});
            skLineSegment(sketch, "E125", {"start": v(-163.49, 25.7) * mm, "end": v(-157.07, 19.3) * mm});
            skLineSegment(sketch, "E126", {"start": v(-156.78, 10.5) * mm, "end": v(-172.28, 10.5) * mm});
            skLineSegment(sketch, "E127", {"start": v(-175.28, 13.5) * mm, "end": v(-175.28, 23) * mm});
            skLineSegment(sketch, "E128", {"start": v(-175.28, 23) * mm, "end": v(-173.28, 23) * mm});
            skLineSegment(sketch, "E129", {"start": v(-173.28, 23) * mm, "end": v(-173.28, 13.5) * mm});
            skLineSegment(sketch, "E130", {"start": v(-172.28, 12.5) * mm, "end": v(-156.78, 12.5) * mm});
            skLineSegment(sketch, "E131.trimOffspring", {"start": v(-156.78, 10.5) * mm, "end": v(-156.78, 10) * mm});
            skPoint(sketch, "E132.visualSharp", {"position": v(-181.78, 26) * mm});
            skArc(sketch, "E132.filletArc", {"start": v(-180.78, 26) * mm, "mid": v(-181.49, 25.7) * mm, "end": v(-181.78, 25) * mm});
            skPoint(sketch, "E133.visualSharp", {"position": v(-181.78, 9) * mm});
            skArc(sketch, "E133.filletArc", {"start": v(-181.78, 10) * mm, "mid": v(-181.49, 9.3) * mm, "end": v(-180.78, 9) * mm});
            skPoint(sketch, "E134.visualSharp", {"position": v(-156.78, 9) * mm});
            skArc(sketch, "E134.filletArc", {"start": v(-157.78, 9) * mm, "mid": v(-157.07, 9.3) * mm, "end": v(-156.78, 10) * mm});
            skPoint(sketch, "E135.visualSharp", {"position": v(-156.78, 19) * mm});
            skArc(sketch, "E135.filletArc", {"start": v(-156.78, 18.59) * mm, "mid": v(-156.86, 18.97) * mm, "end": v(-157.07, 19.3) * mm});
            skPoint(sketch, "E136.visualSharp", {"position": v(-163.78, 26) * mm});
            skArc(sketch, "E136.filletArc", {"start": v(-163.49, 25.7) * mm, "mid": v(-163.81, 25.92) * mm, "end": v(-164.2, 26) * mm});
            skPoint(sketch, "E137.visualSharp", {"position": v(-173.28, 12.5) * mm});
            skArc(sketch, "E137.filletArc", {"start": v(-173.28, 13.5) * mm, "mid": v(-172.99, 12.8) * mm, "end": v(-172.28, 12.5) * mm});
            skPoint(sketch, "E138.visualSharp", {"position": v(-175.28, 10.5) * mm});
            skArc(sketch, "E138.filletArc", {"start": v(-175.28, 13.5) * mm, "mid": v(-174.4, 11.38) * mm, "end": v(-172.28, 10.5) * mm});
            skSolve(sketch);
        }
        {
            var Q0;
            {var subQ2=sQuery(id+"F6.wireOp",EDGE,"E126");Q0=makeQuery(id+"F6.imprint","IMPRINT",FACE,{"disambiguationData":[TD([[makeQuery(id+"F6.imprint","IMPRINT",EDGE,{"derivedFrom":subQ2}),-1.0]])]});}
            extrude(context, id + "F7", {"entities" : qUnion([Q0]), "operationType" : NewBodyOperationType.REMOVE, "oppositeDirection" : true, "depth" : 2 * mm, "offsetDistance" : 25 * mm});
        }
        {
            var Q0;
            Q0=makeQuery(id+"F0.imprint","IMPRINT",FACE,{"disambiguationData":[TD([[makeQuery(id+"F0.imprint","IMPRINT",EDGE,{"derivedFrom":sQuery(id+"F0.wireOp",EDGE,"E91.bottom")}),-1.0]])]});
            extrude(context, id + "F8", {"entities" : qUnion([Q0]), "depth" : 12 * mm, "offsetDistance" : 25 * mm});
        }
        {
            var Q0;
            Q0=makeQuery(id+"F8.opExtrude","CAP_FACE",FACE,{"disambiguationData":[OSD([sQuery(id+"F0.wireOp",EDGE,"E91.bottom"),sQuery(id+"F0.wireOp",EDGE,"E91.top"),sQuery(id+"F0.wireOp",EDGE,"E91.left"),sQuery(id+"F0.wireOp",EDGE,"E91.right"),sQuery(id+"F0.wireOp",EDGE,"E93"),sQuery(id+"F0.wireOp",EDGE,"E94.0.startCap"),sQuery(id+"F0.wireOp",EDGE,"E94.0.endCap"),sQuery(id+"F0.wireOp",EDGE,"E94.0.left"),sQuery(id+"F0.wireOp",EDGE,"E94.0.right"),sQuery(id+"F0.wireOp",EDGE,"E95.filletArc"),sQuery(id+"F0.wireOp",EDGE,"E96.filletArc"),sQuery(id+"F0.wireOp",EDGE,"E97.filletArc"),sQuery(id+"F0.wireOp",EDGE,"E98.filletArc")])],"isStart":false});
            var sketch = newSketch(context, id + "F9", { "sketchPlane" : qUnion([Q0])});
            skLineSegment(sketch, "E139.bottom", {"start": v(-181.5, 74.5) * mm, "end": v(-147.5, 74.5) * mm});
            skLineSegment(sketch, "E139.top", {"start": v(-181.5, 54.5) * mm, "end": v(-179.5, 54.5) * mm});
            skLineSegment(sketch, "E139.left", {"start": v(-182.5, 73.5) * mm, "end": v(-182.5, 55.5) * mm});
            skLineSegment(sketch, "E139.right", {"start": v(-146.5, 73.5) * mm, "end": v(-146.5, 58.5) * mm});
            skLineSegment(sketch, "E140", {"start": v(-149.5, 64.09) * mm, "end": v(-149.5, 58.5) * mm});
            skLineSegment(sketch, "E141", {"start": v(-156.2, 71.21) * mm, "end": v(-149.8, 64.8) * mm});
            skLineSegment(sketch, "E142.trimOffspring", {"start": v(-149.5, 58.5) * mm, "end": v(-146.5, 58.5) * mm});
            skArc(sketch, "E143", {"start": v(-163.84, 71.5) * mm, "mid": v(-170.86, 73.4) * mm, "end": v(-176.98, 69.5) * mm});
            skLineSegment(sketch, "E144.trimOffspring", {"start": v(-163.84, 71.5) * mm, "end": v(-156.92, 71.5) * mm});
            skArc(sketch, "E145", {"start": v(-180.08, 69.5) * mm, "mid": v(-181.18, 63.9) * mm, "end": v(-179.5, 58.43) * mm});
            skLineSegment(sketch, "E146.trimOffspring", {"start": v(-179.5, 58.43) * mm, "end": v(-179.5, 54.5) * mm});
            skLineSegment(sketch, "E147", {"start": v(-176.98, 69.5) * mm, "end": v(-180.08, 69.5) * mm});
            skPoint(sketch, "E148.visualSharp", {"position": v(-182.5, 54.5) * mm});
            skArc(sketch, "E148.filletArc", {"start": v(-182.5, 55.5) * mm, "mid": v(-182.2, 54.8) * mm, "end": v(-181.5, 54.5) * mm});
            skPoint(sketch, "E149.visualSharp", {"position": v(-182.5, 74.5) * mm});
            skArc(sketch, "E149.filletArc", {"start": v(-181.5, 74.5) * mm, "mid": v(-182.2, 74.21) * mm, "end": v(-182.5, 73.5) * mm});
            skPoint(sketch, "E150.visualSharp", {"position": v(-146.5, 74.5) * mm});
            skArc(sketch, "E150.filletArc", {"start": v(-146.5, 73.5) * mm, "mid": v(-146.8, 74.21) * mm, "end": v(-147.5, 74.5) * mm});
            skPoint(sketch, "E151.visualSharp", {"position": v(-146.5, 58.5) * mm});
            skPoint(sketch, "E152.visualSharp", {"position": v(-156.5, 71.5) * mm});
            skArc(sketch, "E152.filletArc", {"start": v(-156.2, 71.21) * mm, "mid": v(-156.53, 71.43) * mm, "end": v(-156.92, 71.5) * mm});
            skPoint(sketch, "E153.visualSharp", {"position": v(-149.5, 64.5) * mm});
            skArc(sketch, "E153.filletArc", {"start": v(-149.5, 64.09) * mm, "mid": v(-149.58, 64.47) * mm, "end": v(-149.8, 64.8) * mm});
            skPoint(sketch, "E154.visualSharp", {"position": v(-149.5, 58.5) * mm});
            skPoint(sketch, "E155.visualSharp", {"position": v(-179.5, 54.5) * mm});
            skSolve(sketch);
        }
        {
            var Q0;
            Q0=makeQuery(id+"F9.imprint","IMPRINT",FACE,{"disambiguationData":[TD([[makeQuery(id+"F9.imprint","IMPRINT",EDGE,{"derivedFrom":sQuery(id+"F9.wireOp",EDGE,"E140")}),-1.0]])]});
            extrude(context, id + "F10", {"entities" : qUnion([Q0]), "operationType" : NewBodyOperationType.REMOVE, "oppositeDirection" : true, "depth" : 9 * mm, "offsetDistance" : 25 * mm});
        }
    });
